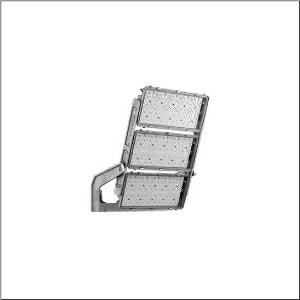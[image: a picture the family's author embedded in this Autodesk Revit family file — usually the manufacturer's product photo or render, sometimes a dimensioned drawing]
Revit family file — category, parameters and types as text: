
# Revit family: floodlight_fl_11_maxi_pro_remote___pl43_5xa779427a01aa_51b3
name_source: partatom
category: Lighting Fixtures
units: mm (PartAtom-declared; Revit-internal decimal feet)

## family parameters
Cut with Voids When Loaded = No
Host = Face
Light Source = No
Part Type = Normal
Room Calculation Point = No
Round Connector Dimension = Use Diameter
Shared = No

## types (1)
- --- (1 x LED, 177380 lm, 1425.5 W, 5000K)
    Apparent Load = 1425 VA
    CIE Flux Codes = 25 74 99 100 100
    Color Rendering = 70
    Color Temperature = 5000K
    Default Elevation = 1800 mm
    Description = Floodlight FL 11  maxi  pro Remote floodlight; light control with lens of PMMA; cover panel of toughened safety glass, transparent; light distribution: PL43, asymmetric direct distribution, LEDcolour temperature: 5000K, rated luminous flux: 177.380lm, colour rendering: CRI > 70, light colour: 750; luminous efficacy: 124lm/W; brightness control: DALI 2 (1 DALI address); with terminal, 8-pole, max. 2.5mm², mains connection: 220..240V/380..400V AC, 50/60Hz, surge voltage resistance: line to ground: 10kV, ECG replaceable separately, LED unit replaceable without ESD environment, dustproof LED module, dimming range 10..100%, no afterglow with DALI off / DMX off command; 1426W floodlight with 2x LED unit of diecast aluminium, coated grey; length: 713mm / width: 651mm / height: 338mm; mounting bracket, of diecast aluminium, uncoated, natural, equipment: Power, protection rating (complete): IP66; insulation class (complete): insulation class I (protective earthing); certification: CE, ENEC, VDE; ball protection: ball impact resistance with accessories, impact resistance: IK07; rated ambient temperature 10°C, only for outdoor installations, permissible operating ambient temperature: -40..+30°C, permissible storage temperature: -40..+85°Cpackaging unit: 1 piece

Light Distribution: PL43
    Height = 320 mm
    Lamp = 1 x LED
    Lamp Light Flux = 177380 lm
    Lamp Power = 1425.5 W
    Lamp count = 1
    Length = 1002 mm
    Luminous efficacy = 124 lm/W
    Manufacturer = Siteco
    ModVariant = No
    Model = 5XA779427A01AA
    Mounting Place = Ceiling
    Mounting Type = Surface mounted
    Number of Poles = 1
    OnlyDefault = Yes
    Power Factor = 1
    Product Name = Floodlight FL 11 maxi pro Remote | PL43
    Product group = floodlight | ceiling mounted
    ProductGroupID = 301
    Protection Class = Protection class I
    Protection Degree = IP 66
    RLX_Detail_Level = 1
    RLX_Emergency_Light_Flux = 0 lm
    RLX_Emergency_Type = 0
    RLX_Emergency_Type_DB = No
    RlxData = <blob elided: 52497 chars, md5=dcd34d70>
    Socket = socket
    Standby Power = 0 W
    System Light Flux = 177380 lm
    System Power = 1425 W
    Type Comments = factory setting: luminous flux: 100 % | dim-lin: 254 | 980 mA
    Type Image = l_1349141.jpg
    URL = http://relux.com
    VarID = @adj_096428
    Voltage = 0 V
    Weight = 0.00 kg
    Width = 655 mm

## geometry (parser evidence)
native form markers: Blend x4, Sweep x15
no freeform markers — native parametric forms only
